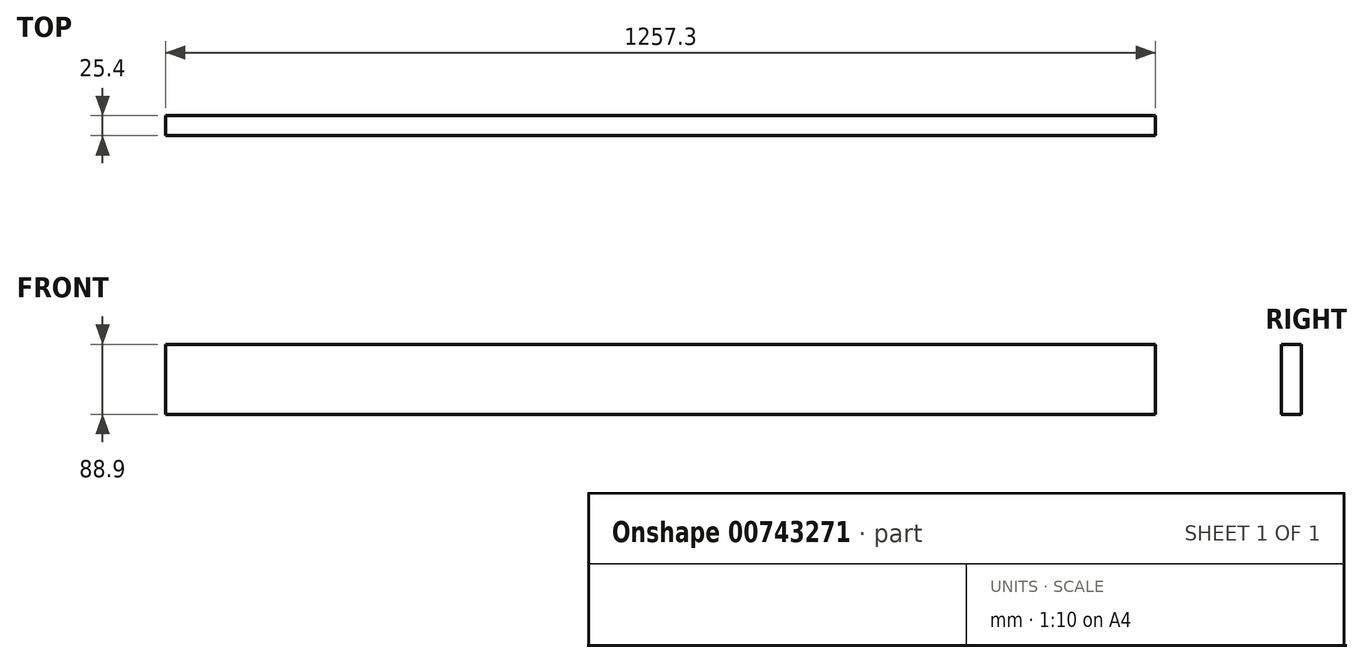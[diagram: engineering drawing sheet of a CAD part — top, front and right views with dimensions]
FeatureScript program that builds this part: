
annotation { "Feature Type Name" : "Feature", "Feature Type Description" : "" }
export const myFeature = defineFeature(function(context is Context, id is Id, definition is map)
    precondition{}
    {
        {
            var Q0;
            Q0=qCreatedBy(makeId("Front.planeOp"),FACE);
            var sketch = newSketch(context, id + "F0", { "sketchPlane" : qUnion([Q0])});
            skLineSegment(sketch, "E0.bottom", {"start": v(0, 0) * mm, "end": v(1257.3, 0) * mm});
            skLineSegment(sketch, "E0.top", {"start": v(0, 88.9) * mm, "end": v(1257.3, 88.9) * mm});
            skLineSegment(sketch, "E0.left", {"start": v(0, 0) * mm, "end": v(0, 88.9) * mm});
            skLineSegment(sketch, "E0.right", {"start": v(1257.3, 0) * mm, "end": v(1257.3, 88.9) * mm});
            skSolve(sketch);
        }
        {
            var Q0;
            Q0 = qSketchRegion(id + "F0", true);
            extrude(context, id + "F1", {"entities" : qUnion([Q0]), "depth" : 25.4 * mm, "offsetDistance" : 25.4 * mm});
        }
    });
